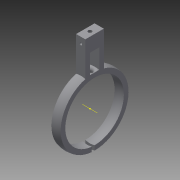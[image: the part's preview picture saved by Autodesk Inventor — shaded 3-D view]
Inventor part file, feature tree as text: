
AUTODESK INVENTOR PART (.ipt)
format: ipt  version: 2015 SP1 (Build 190203100, 203)  size: 193,536 bytes
history: native  units: mm
features: sketch x5, extrude x3, projected_geometry x3, other x1, revolve x1, fillet x1
ambient origin geometry x8: Origin, YZ Plane, XZ Plane, XY Plane, X Axis, Y Axis, Z Axis, Center Point
bodies: Body1 (feature_tree)
feature tree (14):
  other  "Sólido1"
  sketch  "Boceto1"  dims[d0=32.5mm d1=10.0mm]
  revolve  "Revolución1"  [1 undecoded]
  extrude  "Extrusión1"  Depth=5.0mm
  extrude  "Extrusión2"  Depth=10.0mm
  extrude  "Extrusión3"  Depth=20.0mm
  fillet  "Empalme1"  [1 undecoded]
  sketch  "Boceto2"  dims[d2=180.0deg d3=5.0mm]
  sketch  "Boceto3"  dims[d5=61.959188mm d11=10.0mm]
  sketch  "Boceto4"  dims[d12=40.0mm d13=20.0mm d14=90.0deg]
  projected_geometry  "Contorno proyectado1"
  sketch  "Boceto5"  dims[d15=10.0mm d16=0.0mm d17=4.0mm d18=0.0mm d19=0.0mm d20=5.0mm d21=40.0mm d22=0.0mm d23=3.0mm d28=25.0mm d29=25.0mm]
  projected_geometry  "Contorno proyectado2"
  projected_geometry  "Contorno proyectado3"
note: 2 required parameter values undecoded (feature->parameter linkage not recoverable at this tier; creation-order binding heuristic only, values carry confidence <= 0.55)